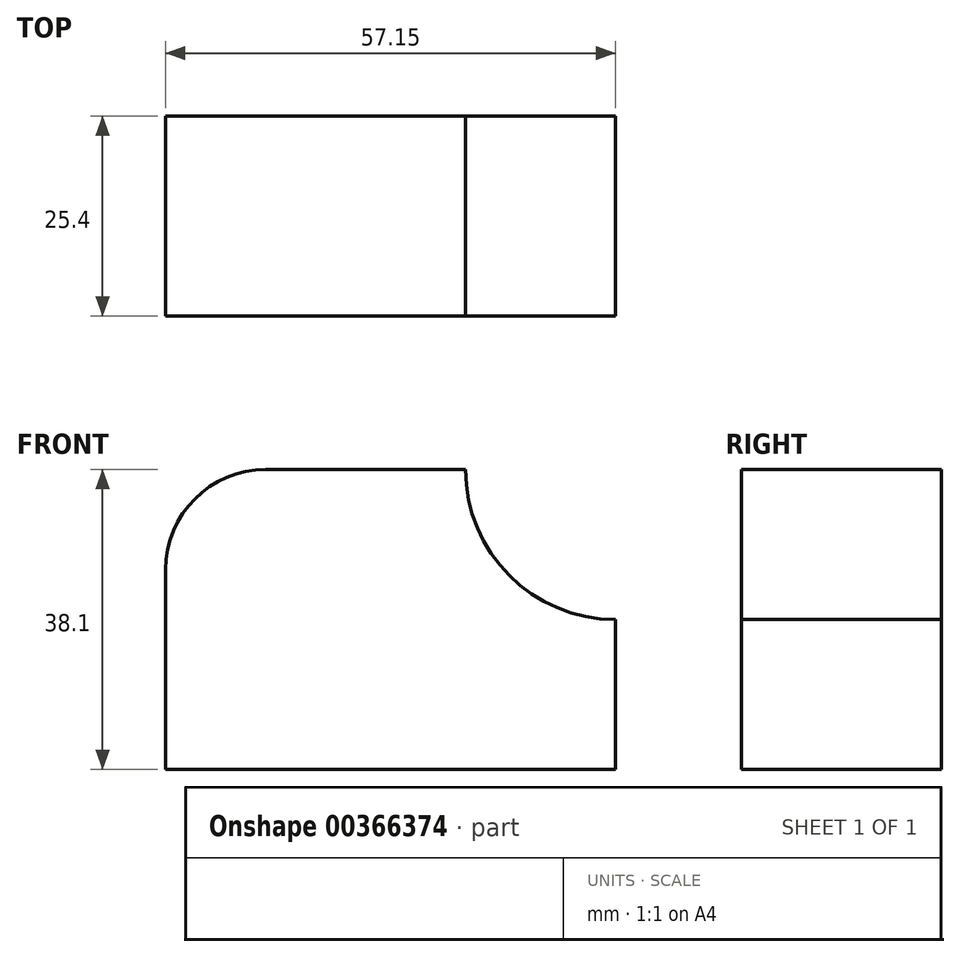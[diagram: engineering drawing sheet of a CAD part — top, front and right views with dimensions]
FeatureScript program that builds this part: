
annotation { "Feature Type Name" : "Feature", "Feature Type Description" : "" }
export const myFeature = defineFeature(function(context is Context, id is Id, definition is map)
    precondition{}
    {
        {
            var Q0;
            Q0=qCreatedBy(makeId("Front.planeOp"),FACE);
            var sketch = newSketch(context, id + "F0", { "sketchPlane" : qUnion([Q0])});
            skLineSegment(sketch, "E0", {"start": v(0, 0) * mm, "end": v(0, 38.1) * mm});
            skLineSegment(sketch, "E1", {"start": v(0, 38.1) * mm, "end": v(38.1, 38.1) * mm});
            skLineSegment(sketch, "E2", {"start": v(0, 0) * mm, "end": v(57.15, 0) * mm});
            skLineSegment(sketch, "E3", {"start": v(57.15, 0) * mm, "end": v(57.15, 19.05) * mm});
            skArc(sketch, "E4", {"start": v(57.15, 19.05) * mm, "mid": v(43.68, 24.63) * mm, "end": v(38.1, 38.1) * mm});
            skSolve(sketch);
        }
        {
            var Q0;
            Q0 = qSketchRegion(id + "F0", true);
            extrude(context, id + "F1", {"entities" : qUnion([Q0]), "depth" : 25.4 * mm});
        }
        {
            var Q0;
            Q0=makeQuery(id+"F1.opExtrude","SWEPT_EDGE",EDGE,{"disambiguationData":[OSD([sQuery(id+"F0.wireOp",EDGE,"E0"),sQuery(id+"F0.wireOp",EDGE,"E1")])]});
            fillet(context, id + "F2", {"entities" : qUnion([Q0]), "radius" : 12.7 * mm, "tangentPropagation" : true, "allowEdgeOverflow" : false});
        }
    });
